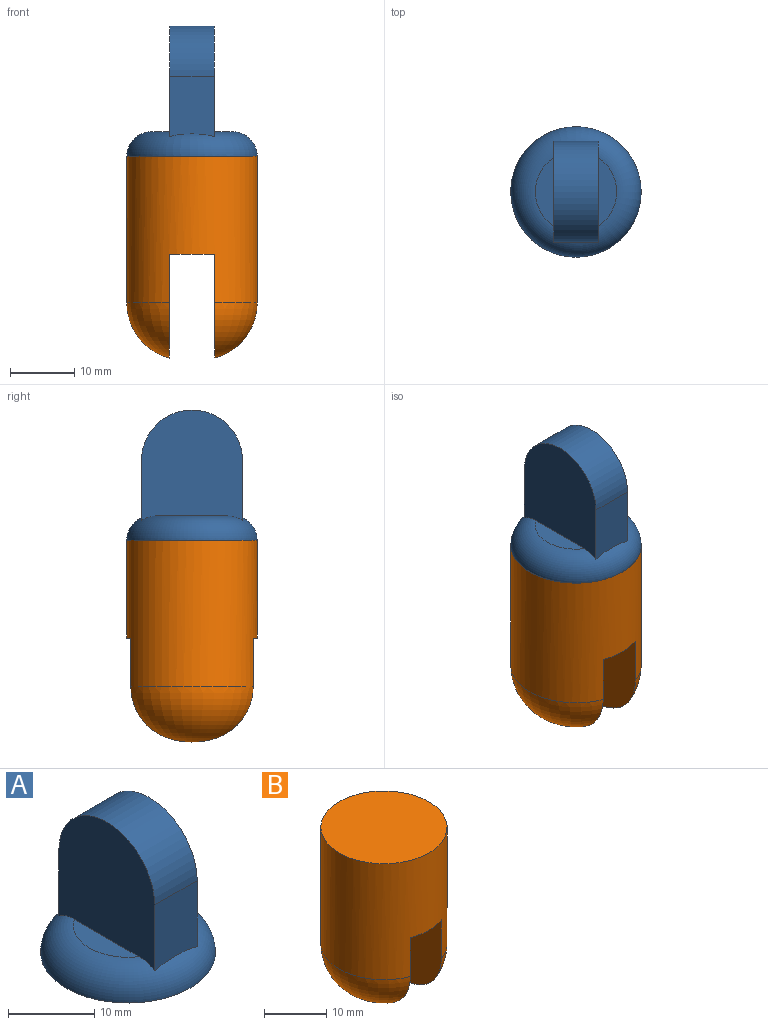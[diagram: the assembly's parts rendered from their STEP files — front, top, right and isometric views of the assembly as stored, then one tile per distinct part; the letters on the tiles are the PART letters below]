
ASSEMBLY  parts=2 mates=1
PART A: 9 faces, bbox 22x22x20.3 mm
  f0: plane 10.61x2.86mm, normal (0,0,1), area 21.3mm2, adj f4,f8
  f1: plane 10.61x2.86mm, normal (0,0,1), area 21.3mm2, adj f6,f8
  f2: plane 20.32x20.32mm, normal (0,0,-1), area 324.3mm2, adj f8
  f3: plane 9.38x6.99mm, normal (0,-1,0), area 63.5mm2, adj f4,f6,f7,f8
  f4: plane 17.26x15.75mm, normal (1,0,0), area 234.6mm2, adj f0,f3,f5,f7,f8
  f5: plane 9.38x6.99mm, normal (0,1,0), area 63.5mm2, adj f4,f6,f7,f8
  f6: plane 17.26x15.75mm, normal (-1,0,0), area 234.6mm2, adj f1,f3,f5,f7,f8
  f7: cylinder r=7.87mm len=15.75mm, axis (-1,0,0), area 172.8mm2, adj f3,f4,f5,f6
  f8: torus R=6.35mm, axis (0,0,1), area 302.9mm2, adj f0,f1,f2,f3,f4,f5,f6
PART B: 7 faces, bbox 20.3x20.3x31.5 mm
  f0: plane 20.32x7.07mm, normal (0,0,-1), area 140.7mm2, adj f1,f3,f4
  f1: cylinder r=10.16mm len=22.86mm, axis (0,0,-1), area 1349.3mm2, adj f0,f2,f3,f4,f5,f6
  f2: plane 20.32x20.32mm, normal (0,0,1), area 324.3mm2, adj f1
  f3: plane 19.05x16.22mm, normal (1,0,0), area 275.5mm2, adj f0,f1,f6
  f4: plane 19.05x16.22mm, normal (-1,0,0), area 275.6mm2, adj f0,f1,f5
  f5: torus R=1.27mm, axis (0,0,-1), area 199.1mm2, adj f1,f4
  f6: torus R=1.27mm, axis (0,0,-1), area 199.1mm2, adj f1,f3
PLACE A t=(-23.63,-1.83,-6.41)mm
PLACE B t=(-23.63,-1.83,-21.65)mm
MATE fastened B.f1 <-> A.f8  axis (0,0,1) through (-23.63,-1.83,-6.41)mm
